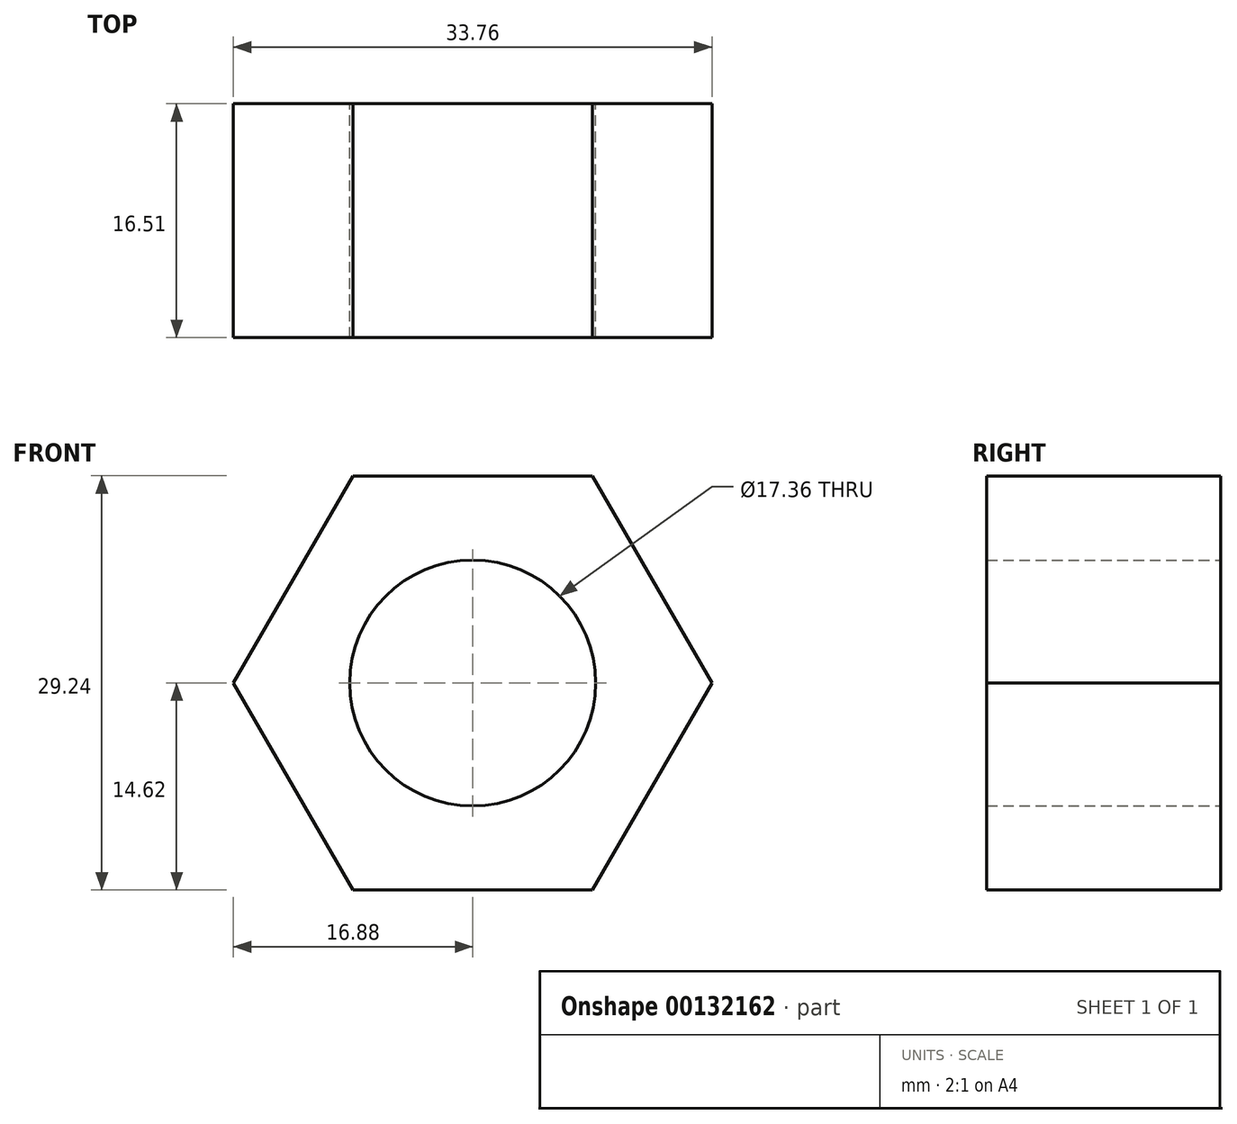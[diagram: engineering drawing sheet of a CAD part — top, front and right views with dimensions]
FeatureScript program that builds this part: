
annotation { "Feature Type Name" : "Feature", "Feature Type Description" : "" }
export const myFeature = defineFeature(function(context is Context, id is Id, definition is map)
    precondition{}
    {
        {
            var Q0;
            Q0=qCreatedBy(makeId("Front.planeOp"),FACE);
            var sketch = newSketch(context, id + "F0", { "sketchPlane" : qUnion([Q0])});
            skCircle(sketch, "E0.cCircle", {"center": v(0, 0) * mm, "radius": 14.62 * mm, "construction": true});
            skLineSegment(sketch, "E0.0", {"start": v(8.44, -14.62) * mm, "end": v(-8.44, -14.62) * mm});
            skLineSegment(sketch, "E0.1", {"start": v(-8.44, -14.62) * mm, "end": v(-16.88, 0) * mm});
            skLineSegment(sketch, "E0.2", {"start": v(-16.88, 0) * mm, "end": v(-8.44, 14.62) * mm});
            skLineSegment(sketch, "E0.3", {"start": v(-8.44, 14.62) * mm, "end": v(8.44, 14.62) * mm});
            skLineSegment(sketch, "E0.4", {"start": v(8.44, 14.62) * mm, "end": v(16.88, 0) * mm});
            skLineSegment(sketch, "E0.5", {"start": v(16.88, 0) * mm, "end": v(8.44, -14.62) * mm});
            skPoint(sketch, "E0.0.midPoint", {"position": v(0, -14.62) * mm});
            skCircle(sketch, "E1", {"center": v(0, 0) * mm, "radius": 8.68 * mm});
            skSolve(sketch);
        }
        {
            var Q0;
            Q0=makeQuery(id+"F0.imprint","IMPRINT",FACE,{"disambiguationData":[TD([[makeQuery(id+"F0.imprint","IMPRINT",EDGE,{"derivedFrom":sQuery(id+"F0.wireOp",EDGE,"E0.0")}),-1.0]])]});
            extrude(context, id + "F1", {"entities" : qUnion([Q0]), "depth" : 16.5 * mm});
        }
    });
